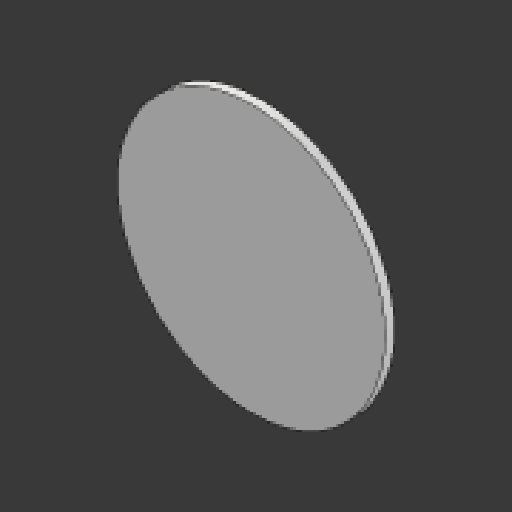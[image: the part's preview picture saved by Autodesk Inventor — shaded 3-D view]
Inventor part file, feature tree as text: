
AUTODESK INVENTOR PART (.ipt)
format: ipt  version: 2023 (Build 270158000, 158)  size: 79,360 bytes
history: native  units: mm
features: extrude x1, sketch x1
ambient origin geometry x8: Origin, YZ Plane, XZ Plane, XY Plane, X Axis, Y Axis, Z Axis, Center Point
bodies: Solid1 (feature_tree)
feature tree (2):
  extrude  "Extrusion1"  Depth=2.0mm TaperAngle=0.0deg
  sketch  "Sketch1"  dims[d0=60.0mm d1=2.0mm d2=0.0mm]
